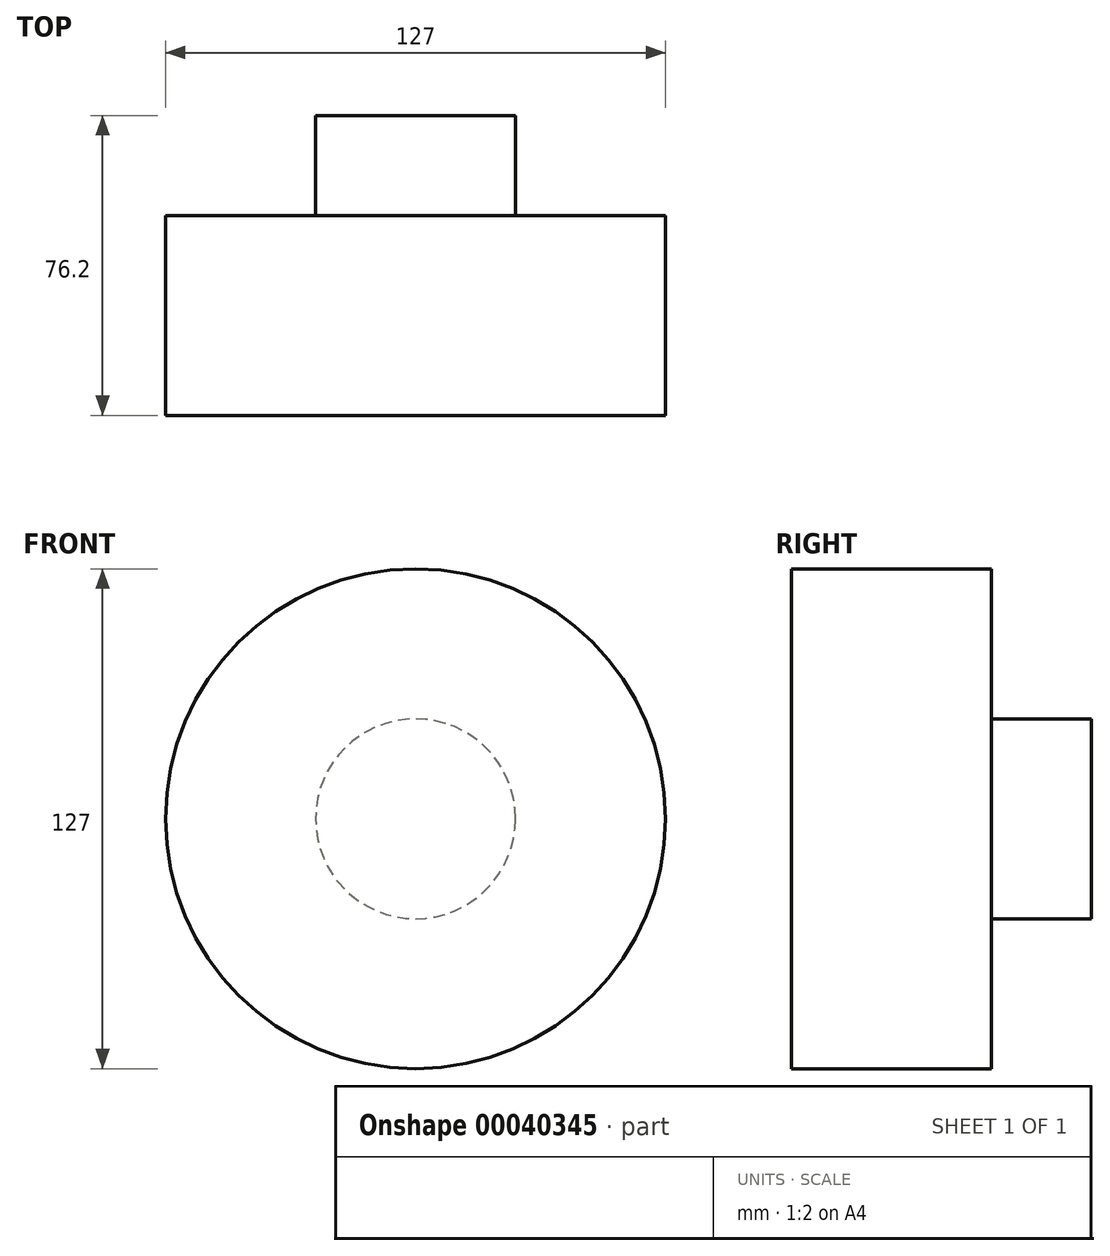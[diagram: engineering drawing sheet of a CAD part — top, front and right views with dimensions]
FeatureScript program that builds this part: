
annotation { "Feature Type Name" : "Feature", "Feature Type Description" : "" }
export const myFeature = defineFeature(function(context is Context, id is Id, definition is map)
    precondition{}
    {
        {
            var Q0;
            Q0=qCreatedBy(makeId("Right.planeOp"),FACE);
            var sketch = newSketch(context, id + "F0", { "sketchPlane" : qUnion([Q0])});
            skLineSegment(sketch, "E0", {"start": v(-27.87, 60.6) * mm, "end": v(-27.87, 33.31) * mm});
            skLineSegment(sketch, "E1", {"start": v(22.35, 60.6) * mm, "end": v(22.35, 22.5) * mm});
            skLineSegment(sketch, "E2", {"start": v(22.35, 22.5) * mm, "end": v(47.75, 22.5) * mm});
            skLineSegment(sketch, "E3", {"start": v(47.75, 22.5) * mm, "end": v(47.75, -2.9) * mm});
            skLineSegment(sketch, "E4", {"start": v(47.75, -2.9) * mm, "end": v(-28.45, -2.9) * mm});
            skLineSegment(sketch, "E5", {"start": v(-28.45, -2.9) * mm, "end": v(-28.45, 33.31) * mm});
            skLineSegment(sketch, "E6", {"start": v(-28.45, 33.31) * mm, "end": v(-28.45, 60.6) * mm});
            skLineSegment(sketch, "E7", {"start": v(-28.45, 60.6) * mm, "end": v(22.35, 60.6) * mm});
            skSolve(sketch);
        }
        {
            var Q0;
            {var subQ1=sQuery(id+"F0.wireOp",EDGE,"E1");Q0=makeQuery(id+"F0.imprint","IMPRINT",FACE,{"disambiguationData":[TD([[makeQuery(id+"F0.imprint","IMPRINT",EDGE,{"derivedFrom":subQ1}),-1.0]])]});}
            var Q1;
            Q1=sQuery(id+"F0.wireOp",EDGE,"E4");
            revolve(context, id + "F1", {"entities" : qUnion([Q0]), "axis" : qUnion([Q1]), "revolveType" : RevolveType.FULL});
        }
    });
